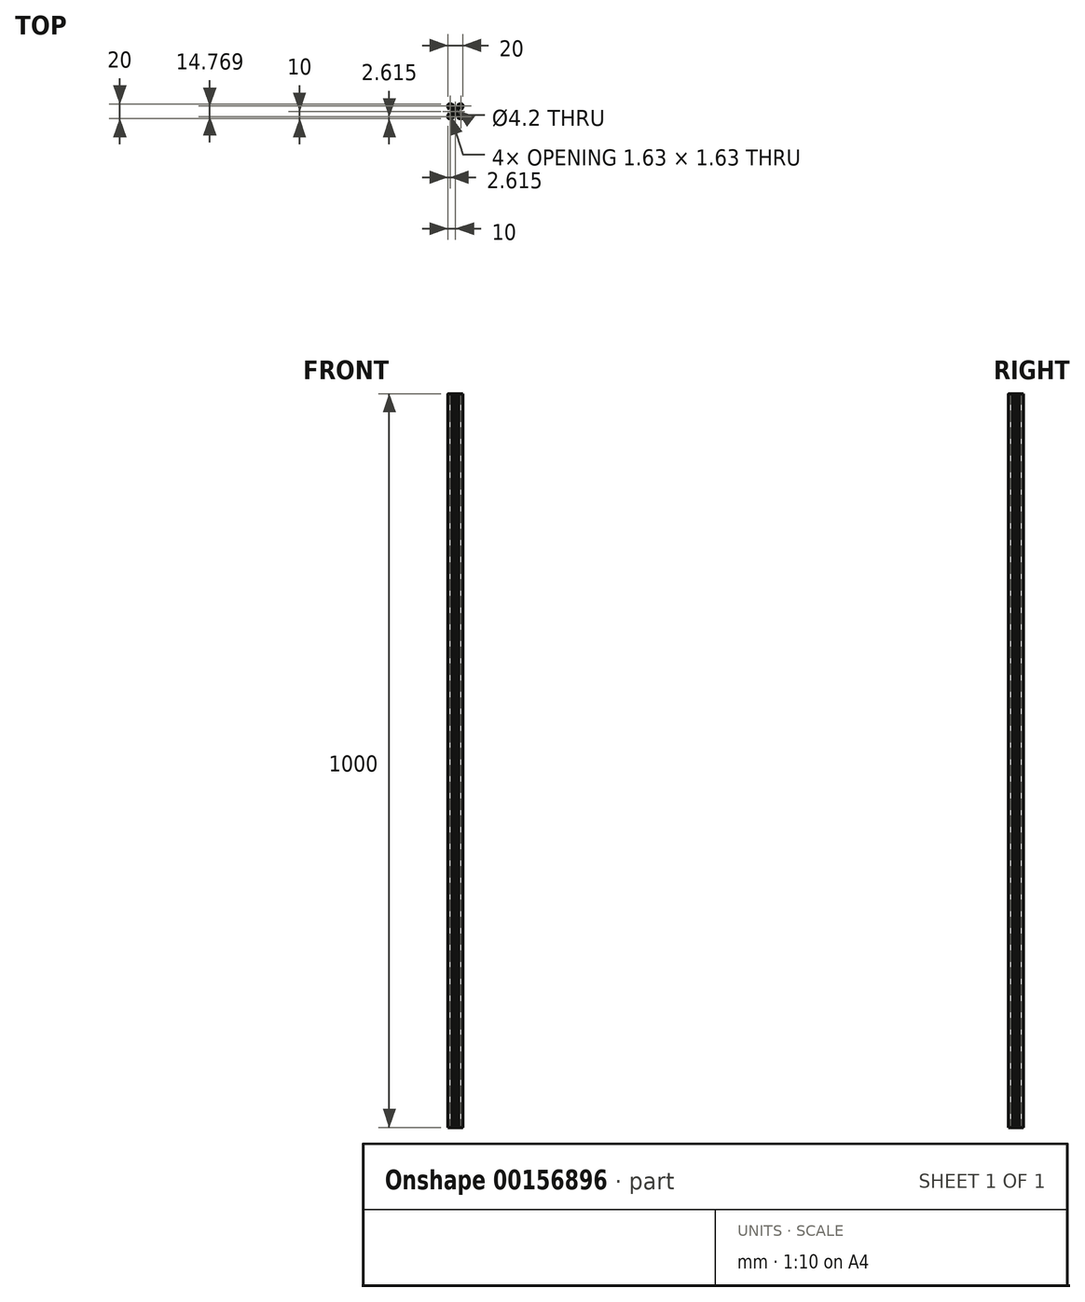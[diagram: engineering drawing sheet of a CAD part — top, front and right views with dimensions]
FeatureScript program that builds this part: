
annotation { "Feature Type Name" : "Feature", "Feature Type Description" : "" }
export const myFeature = defineFeature(function(context is Context, id is Id, definition is map)
    precondition{}
    {
        {
            var Q0;
            Q0=qCreatedBy(makeId("Top.planeOp"),FACE);
            var sketch = newSketch(context, id + "F0", { "sketchPlane" : qUnion([Q0])});
            skArc(sketch, "E0", {"start": v(-8.5, 10) * mm, "mid": v(-9.56, 9.56) * mm, "end": v(-10, 8.5) * mm});
            skLineSegment(sketch, "E1", {"start": v(-10, 8.5) * mm, "end": v(-10, 4.64) * mm});
            skLineSegment(sketch, "E2", {"start": v(-10, 4.64) * mm, "end": v(-8.2, 2.84) * mm});
            skLineSegment(sketch, "E3", {"start": v(-8.2, 5.5) * mm, "end": v(-8.2, 2.84) * mm});
            skLineSegment(sketch, "E4", {"start": v(-8.2, 5.5) * mm, "end": v(-6.56, 5.5) * mm});
            skLineSegment(sketch, "E5", {"start": v(-6.56, 5.5) * mm, "end": v(-3.9, 2.84) * mm});
            skLineSegment(sketch, "E6", {"start": v(-3.9, 2.84) * mm, "end": v(-3.9, 0.2) * mm});
            skLineSegment(sketch, "E7", {"start": v(-3.9, 0.2) * mm, "end": v(-3.7, 0) * mm});
            skLineSegment(sketch, "E8", {"start": v(-3.9, -0.2) * mm, "end": v(-3.7, 0) * mm});
            skLineSegment(sketch, "E9", {"start": v(-3.9, -2.84) * mm, "end": v(-3.9, -0.2) * mm});
            skLineSegment(sketch, "E10", {"start": v(-6.56, -5.5) * mm, "end": v(-3.9, -2.84) * mm});
            skLineSegment(sketch, "E11", {"start": v(-8.2, -5.5) * mm, "end": v(-6.56, -5.5) * mm});
            skLineSegment(sketch, "E12", {"start": v(-8.2, -5.5) * mm, "end": v(-8.2, -2.84) * mm});
            skLineSegment(sketch, "E13", {"start": v(-10, -4.64) * mm, "end": v(-8.2, -2.84) * mm});
            skLineSegment(sketch, "E14", {"start": v(-10, -8.5) * mm, "end": v(-10, -4.64) * mm});
            skArc(sketch, "E15", {"start": v(-10, -8.5) * mm, "mid": v(-9.56, -9.56) * mm, "end": v(-8.5, -10) * mm});
            skLineSegment(sketch, "E16", {"start": v(-8.5, -10) * mm, "end": v(-4.64, -10) * mm});
            skLineSegment(sketch, "E17", {"start": v(-4.64, -10) * mm, "end": v(-2.84, -8.2) * mm});
            skLineSegment(sketch, "E18", {"start": v(-2.84, -8.2) * mm, "end": v(-5.5, -8.2) * mm});
            skLineSegment(sketch, "E19", {"start": v(-5.5, -8.2) * mm, "end": v(-5.5, -6.56) * mm});
            skLineSegment(sketch, "E20", {"start": v(-5.5, -6.56) * mm, "end": v(-2.84, -3.9) * mm});
            skLineSegment(sketch, "E21", {"start": v(-0.2, -3.9) * mm, "end": v(-2.84, -3.9) * mm});
            skLineSegment(sketch, "E22", {"start": v(-0.2, -3.9) * mm, "end": v(0, -3.7) * mm});
            skLineSegment(sketch, "E23", {"start": v(0.2, -3.9) * mm, "end": v(0, -3.7) * mm});
            skLineSegment(sketch, "E24", {"start": v(0.2, -3.9) * mm, "end": v(2.84, -3.9) * mm});
            skLineSegment(sketch, "E25", {"start": v(5.5, -6.56) * mm, "end": v(2.84, -3.9) * mm});
            skLineSegment(sketch, "E26", {"start": v(5.5, -8.2) * mm, "end": v(5.5, -6.56) * mm});
            skLineSegment(sketch, "E27", {"start": v(2.84, -8.2) * mm, "end": v(5.5, -8.2) * mm});
            skLineSegment(sketch, "E28", {"start": v(4.64, -10) * mm, "end": v(2.84, -8.2) * mm});
            skLineSegment(sketch, "E29", {"start": v(8.5, -10) * mm, "end": v(4.64, -10) * mm});
            skArc(sketch, "E30", {"start": v(8.5, -10) * mm, "mid": v(9.56, -9.56) * mm, "end": v(10, -8.5) * mm});
            skLineSegment(sketch, "E31", {"start": v(10, -8.5) * mm, "end": v(10, -4.64) * mm});
            skLineSegment(sketch, "E32", {"start": v(10, -4.64) * mm, "end": v(8.2, -2.84) * mm});
            skLineSegment(sketch, "E33", {"start": v(8.2, -5.5) * mm, "end": v(8.2, -2.84) * mm});
            skLineSegment(sketch, "E34", {"start": v(8.2, -5.5) * mm, "end": v(6.56, -5.5) * mm});
            skLineSegment(sketch, "E35", {"start": v(6.56, -5.5) * mm, "end": v(3.9, -2.84) * mm});
            skLineSegment(sketch, "E36", {"start": v(3.9, -2.84) * mm, "end": v(3.9, -0.2) * mm});
            skLineSegment(sketch, "E37", {"start": v(3.9, -0.2) * mm, "end": v(3.7, 0) * mm});
            skLineSegment(sketch, "E38", {"start": v(3.9, 0.2) * mm, "end": v(3.7, 0) * mm});
            skLineSegment(sketch, "E39", {"start": v(3.9, 2.84) * mm, "end": v(3.9, 0.2) * mm});
            skLineSegment(sketch, "E40", {"start": v(6.56, 5.5) * mm, "end": v(3.9, 2.84) * mm});
            skLineSegment(sketch, "E41", {"start": v(8.2, 5.5) * mm, "end": v(6.56, 5.5) * mm});
            skLineSegment(sketch, "E42", {"start": v(8.2, 5.5) * mm, "end": v(8.2, 2.84) * mm});
            skLineSegment(sketch, "E43", {"start": v(10, 4.64) * mm, "end": v(8.2, 2.84) * mm});
            skLineSegment(sketch, "E44", {"start": v(10, 8.5) * mm, "end": v(10, 4.64) * mm});
            skArc(sketch, "E45", {"start": v(10, 8.5) * mm, "mid": v(9.56, 9.56) * mm, "end": v(8.5, 10) * mm});
            skLineSegment(sketch, "E46", {"start": v(8.5, 10) * mm, "end": v(4.64, 10) * mm});
            skLineSegment(sketch, "E47", {"start": v(4.64, 10) * mm, "end": v(2.84, 8.2) * mm});
            skLineSegment(sketch, "E48", {"start": v(2.84, 8.2) * mm, "end": v(5.5, 8.2) * mm});
            skLineSegment(sketch, "E49", {"start": v(5.5, 8.2) * mm, "end": v(5.5, 6.56) * mm});
            skLineSegment(sketch, "E50", {"start": v(5.5, 6.56) * mm, "end": v(2.84, 3.9) * mm});
            skLineSegment(sketch, "E51", {"start": v(0.2, 3.9) * mm, "end": v(2.84, 3.9) * mm});
            skLineSegment(sketch, "E52", {"start": v(0.2, 3.9) * mm, "end": v(0, 3.7) * mm});
            skLineSegment(sketch, "E53", {"start": v(-0.2, 3.9) * mm, "end": v(0, 3.7) * mm});
            skLineSegment(sketch, "E54", {"start": v(-0.2, 3.9) * mm, "end": v(-2.84, 3.9) * mm});
            skLineSegment(sketch, "E55", {"start": v(-5.5, 6.56) * mm, "end": v(-2.84, 3.9) * mm});
            skLineSegment(sketch, "E56", {"start": v(-5.5, 8.2) * mm, "end": v(-5.5, 6.56) * mm});
            skLineSegment(sketch, "E57", {"start": v(-2.84, 8.2) * mm, "end": v(-5.5, 8.2) * mm});
            skLineSegment(sketch, "E58", {"start": v(-4.64, 10) * mm, "end": v(-2.84, 8.2) * mm});
            skLineSegment(sketch, "E59", {"start": v(-8.5, 10) * mm, "end": v(-4.64, 10) * mm});
            skCircle(sketch, "E60", {"center": v(0, 0) * mm, "radius": 2.1 * mm});
            skLineSegment(sketch, "E61", {"start": v(-6.57, 8.2) * mm, "end": v(-8.2, 8.2) * mm});
            skLineSegment(sketch, "E62", {"start": v(-6.57, 8.2) * mm, "end": v(-6.57, 7.63) * mm});
            skLineSegment(sketch, "E63", {"start": v(-7.63, 6.57) * mm, "end": v(-6.57, 7.63) * mm});
            skLineSegment(sketch, "E64", {"start": v(-8.2, 6.57) * mm, "end": v(-7.63, 6.57) * mm});
            skLineSegment(sketch, "E65", {"start": v(-8.2, 8.2) * mm, "end": v(-8.2, 6.57) * mm});
            skLineSegment(sketch, "E66", {"start": v(8.2, 8.2) * mm, "end": v(8.2, 6.57) * mm});
            skLineSegment(sketch, "E67", {"start": v(8.2, 6.57) * mm, "end": v(7.63, 6.57) * mm});
            skLineSegment(sketch, "E68", {"start": v(7.63, 6.57) * mm, "end": v(6.57, 7.63) * mm});
            skLineSegment(sketch, "E69", {"start": v(6.57, 8.2) * mm, "end": v(6.57, 7.63) * mm});
            skLineSegment(sketch, "E70", {"start": v(6.57, 8.2) * mm, "end": v(8.2, 8.2) * mm});
            skLineSegment(sketch, "E71", {"start": v(-8.2, -8.2) * mm, "end": v(-8.2, -6.57) * mm});
            skLineSegment(sketch, "E72", {"start": v(-8.2, -6.57) * mm, "end": v(-7.63, -6.57) * mm});
            skLineSegment(sketch, "E73", {"start": v(-7.63, -6.57) * mm, "end": v(-6.57, -7.63) * mm});
            skLineSegment(sketch, "E74", {"start": v(-6.57, -8.2) * mm, "end": v(-6.57, -7.63) * mm});
            skLineSegment(sketch, "E75", {"start": v(-6.57, -8.2) * mm, "end": v(-8.2, -8.2) * mm});
            skLineSegment(sketch, "E76", {"start": v(6.57, -8.2) * mm, "end": v(8.2, -8.2) * mm});
            skLineSegment(sketch, "E77", {"start": v(6.57, -8.2) * mm, "end": v(6.57, -7.63) * mm});
            skLineSegment(sketch, "E78", {"start": v(7.63, -6.57) * mm, "end": v(6.57, -7.63) * mm});
            skLineSegment(sketch, "E79", {"start": v(8.2, -6.57) * mm, "end": v(7.63, -6.57) * mm});
            skLineSegment(sketch, "E80", {"start": v(8.2, -8.2) * mm, "end": v(8.2, -6.57) * mm});
            skSolve(sketch);
        }
        {
            var Q0;
            Q0=makeQuery(id+"F0.imprint","IMPRINT",FACE,{"disambiguationData":[TD([[makeQuery(id+"F0.imprint","IMPRINT",EDGE,{"derivedFrom":sQuery(id+"F0.wireOp",EDGE,"E0")}),1.0]])]});
            extrude(context, id + "F1", {"entities" : qUnion([Q0]), "depth" : 1000 * mm});
        }
    });
